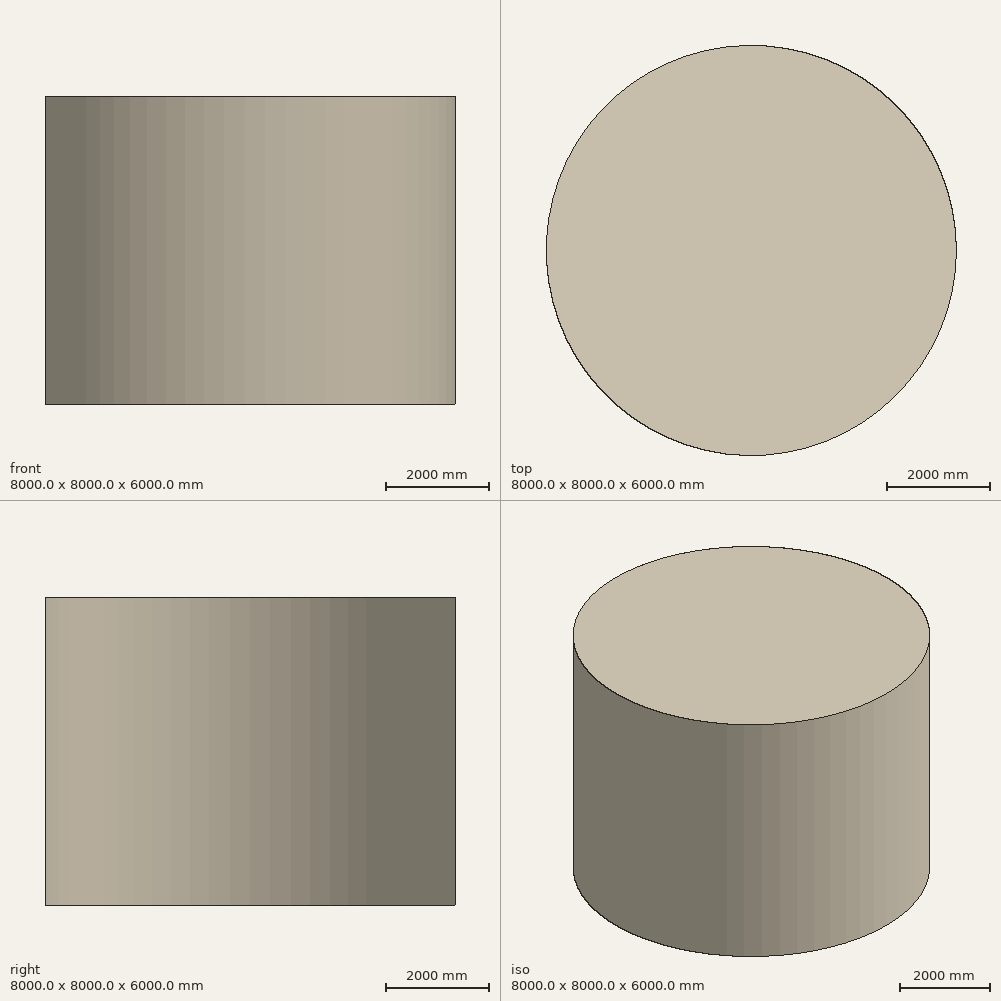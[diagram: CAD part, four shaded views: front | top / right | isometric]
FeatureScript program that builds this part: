
annotation { "Feature Type Name" : "Feature", "Feature Type Description" : "" }
export const myFeature = defineFeature(function(context is Context, id is Id, definition is map)
    precondition{}
    {
        {
            var Q0;
            Q0=qCreatedBy(makeId("Top.planeOp"),FACE);
            var sketch = newSketch(context, id + "F0", { "sketchPlane" : qUnion([Q0])});
            skCircle(sketch, "E0", {"center": v(0, 0) * mm, "radius": 4000 * mm});
            skSolve(sketch);
        }
        {
            var Q0;
            Q0=makeQuery(id+"F0.imprint","IMPRINT",FACE,{"disambiguationData":[TD([[makeQuery(id+"F0.imprint","IMPRINT",EDGE,{"derivedFrom":sQuery(id+"F0.wireOp",EDGE,"E0")}),1.0]])]});
            extrude(context, id + "F1", {"entities" : qUnion([Q0]), "oppositeDirection" : true, "depth" : 6000 * mm, "offsetDistance" : 25 * mm});
        }
    });
